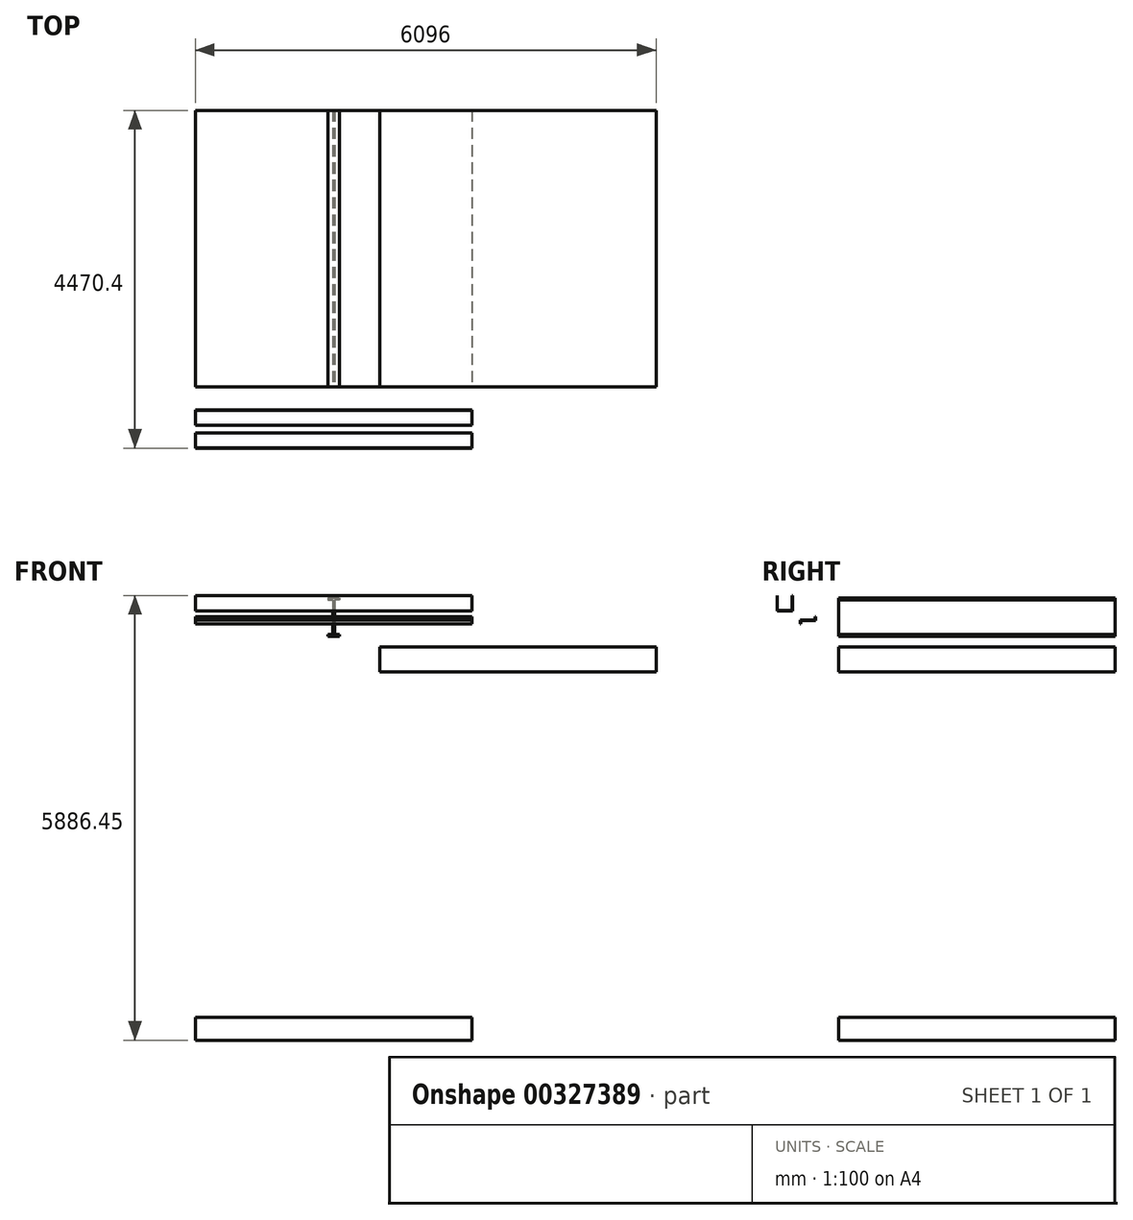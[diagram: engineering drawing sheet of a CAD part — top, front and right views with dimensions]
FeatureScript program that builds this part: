
annotation { "Feature Type Name" : "Feature", "Feature Type Description" : "" }
export const myFeature = defineFeature(function(context is Context, id is Id, definition is map)
    precondition{}
    {
        {
            var Q0;
            Q0=qCreatedBy(makeId("Front.planeOp"), FACE);
            var sketch = newSketch(context, id + "F0", { "sketchPlane" : qUnion([Q0])});
            skLineSegment(sketch, "E0.bottom", {"start": v(-1828.8, 0) * mm, "end": v(1828.8, 0) * mm});
            skLineSegment(sketch, "E0.top", {"start": v(-1828.8, -304.8) * mm, "end": v(1828.8, -304.8) * mm});
            skLineSegment(sketch, "E0.left", {"start": v(-1828.8, 0) * mm, "end": v(-1828.8, -304.8) * mm});
            skLineSegment(sketch, "E0.right", {"start": v(1828.8, 0) * mm, "end": v(1828.8, -304.8) * mm});
            skSolve(sketch);
        }
        {
            var Q0;
            Q0 = qSketchRegion(id + "F0", true);
            extrude(context, id + "F1", {"entities" : qUnion([Q0]), "oppositeDirection" : true, "depth" : 3657.6 * mm, "offsetDistance" : 25.4 * mm});
        }
        {
            var Q0;
            Q0=qCreatedBy(makeId("Front.planeOp"), FACE);
            var sketch = newSketch(context, id + "F2", { "sketchPlane" : qUnion([Q0])});
            skLineSegment(sketch, "E1.bottom", {"start": v(0, 5549.9) * mm, "end": v(76.2, 5549.9) * mm});
            skLineSegment(sketch, "E1.top", {"start": v(0, 5041.9) * mm, "end": v(76.2, 5041.9) * mm});
            skLineSegment(sketch, "E1.left", {"start": v(0, 5549.9) * mm, "end": v(0, 5041.9) * mm, "construction": true});
            skLineSegment(sketch, "E1.right", {"start": v(76.2, 5549.9) * mm, "end": v(76.2, 5524.5) * mm});
            skLineSegment(sketch, "E2.bottom", {"start": v(76.2, 5524.5) * mm, "end": v(12.7, 5524.5) * mm});
            skLineSegment(sketch, "E2.top", {"start": v(76.2, 5067.3) * mm, "end": v(12.7, 5067.3) * mm});
            skLineSegment(sketch, "E2.right", {"start": v(12.7, 5524.5) * mm, "end": v(12.7, 5067.3) * mm});
            skLineSegment(sketch, "E3.trimOffspring", {"start": v(76.2, 5067.3) * mm, "end": v(76.2, 5041.9) * mm});
            skLineSegment(sketch, "E4.MirrorCS", {"start": v(-76.2, 5549.9) * mm, "end": v(-76.2, 5524.5) * mm});
            skLineSegment(sketch, "E5.MirrorCS", {"start": v(-12.7, 5524.5) * mm, "end": v(-12.7, 5067.3) * mm});
            skLineSegment(sketch, "E6.MirrorCS", {"start": v(0, 5549.9) * mm, "end": v(-76.2, 5549.9) * mm});
            skLineSegment(sketch, "E7.MirrorCS", {"start": v(-76.2, 5067.3) * mm, "end": v(-76.2, 5041.9) * mm});
            skLineSegment(sketch, "E8.MirrorCS", {"start": v(0, 5041.9) * mm, "end": v(-76.2, 5041.9) * mm});
            skLineSegment(sketch, "E9.MirrorCS", {"start": v(-76.2, 5524.5) * mm, "end": v(-12.7, 5524.5) * mm});
            skLineSegment(sketch, "E10.MirrorCS", {"start": v(-76.2, 5067.3) * mm, "end": v(-12.7, 5067.3) * mm});
            skSolve(sketch);
        }
        {
            var Q0;
            Q0 = qSketchRegion(id + "F2", true);
            extrude(context, id + "F3", {"entities" : qUnion([Q0]), "oppositeDirection" : true, "depth" : 3657.6 * mm, "offsetDistance" : 25.4 * mm});
        }
        {
            var Q0;
            Q0=qCreatedBy(makeId("Right.planeOp"), FACE);
            var sketch = newSketch(context, id + "F4", { "sketchPlane" : qUnion([Q0])});
            skLineSegment(sketch, "E11.bottom", {"start": v(-508, 5207) * mm, "end": v(-501.65, 5207) * mm});
            skLineSegment(sketch, "E11.left", {"start": v(-508, 5207) * mm, "end": v(-508, 5251.45) * mm});
            skLineSegment(sketch, "E11.right", {"start": v(-501.65, 5207) * mm, "end": v(-501.65, 5251.45) * mm});
            skLineSegment(sketch, "E12.bottom", {"start": v(-501.65, 5251.45) * mm, "end": v(-311.15, 5251.45) * mm});
            skLineSegment(sketch, "E12.top", {"start": v(-508, 5257.8) * mm, "end": v(-311.15, 5257.8) * mm});
            skLineSegment(sketch, "E12.left", {"start": v(-508, 5251.45) * mm, "end": v(-508, 5257.8) * mm});
            skLineSegment(sketch, "E13.bottom", {"start": v(-311.15, 5251.45) * mm, "end": v(-304.8, 5251.45) * mm});
            skLineSegment(sketch, "E13.top", {"start": v(-311.15, 5302.25) * mm, "end": v(-304.8, 5302.25) * mm});
            skLineSegment(sketch, "E13.left", {"start": v(-311.15, 5257.8) * mm, "end": v(-311.15, 5302.25) * mm});
            skLineSegment(sketch, "E13.right", {"start": v(-304.8, 5251.45) * mm, "end": v(-304.8, 5302.25) * mm});
            skSolve(sketch);
        }
        {
            var Q0;
            Q0 = qSketchRegion(id + "F4", true);
            extrude(context, id + "F5", {"entities" : qUnion([Q0]), "depth" : 3657.6 * mm, "offsetDistance" : 25.4 * mm, "symmetric" : true});
        }
        {
            var Q0;
            Q0=qCreatedBy(makeId("Right.planeOp"), FACE);
            var sketch = newSketch(context, id + "F6", { "sketchPlane" : qUnion([Q0])});
            skLineSegment(sketch, "E14.bottom", {"start": v(-812.8, 5581.65) * mm, "end": v(-810.26, 5581.65) * mm});
            skLineSegment(sketch, "E14.top", {"start": v(-812.8, 5378.45) * mm, "end": v(-609.6, 5378.45) * mm});
            skLineSegment(sketch, "E14.left", {"start": v(-812.8, 5581.65) * mm, "end": v(-812.8, 5378.45) * mm});
            skLineSegment(sketch, "E14.right", {"start": v(-609.6, 5581.65) * mm, "end": v(-609.6, 5378.45) * mm});
            skLineSegment(sketch, "E15.top", {"start": v(-810.26, 5381) * mm, "end": v(-612.14, 5381) * mm});
            skLineSegment(sketch, "E15.left", {"start": v(-810.26, 5581.65) * mm, "end": v(-810.26, 5381) * mm});
            skLineSegment(sketch, "E15.right", {"start": v(-612.14, 5581.65) * mm, "end": v(-612.14, 5381) * mm});
            skLineSegment(sketch, "E16.trimOffspring", {"start": v(-612.14, 5581.65) * mm, "end": v(-609.6, 5581.65) * mm});
            skLineSegment(sketch, "E17", {"start": v(-810.26, 5381) * mm, "end": v(-810.26, 5378.45) * mm, "construction": true});
            skSolve(sketch);
        }
        {
            var Q0;
            Q0 = qSketchRegion(id + "F6", true);
            extrude(context, id + "F7", {"entities" : qUnion([Q0]), "depth" : 3657.6 * mm, "offsetDistance" : 25.4 * mm, "symmetric" : true});
        }
        {
            var Q0;
            Q0=qCreatedBy(makeId("Front.planeOp"), FACE);
            var sketch = newSketch(context, id + "F8", { "sketchPlane" : qUnion([Q0])});
            skLineSegment(sketch, "E18.bottom", {"start": v(609.6, 4902.2) * mm, "end": v(4267.2, 4902.2) * mm});
            skLineSegment(sketch, "E18.top", {"start": v(609.6, 4572) * mm, "end": v(4267.2, 4572) * mm});
            skLineSegment(sketch, "E18.left", {"start": v(609.6, 4902.2) * mm, "end": v(609.6, 4572) * mm});
            skLineSegment(sketch, "E18.right", {"start": v(4267.2, 4902.2) * mm, "end": v(4267.2, 4572) * mm});
            skSolve(sketch);
        }
        {
            var Q0;
            Q0 = qSketchRegion(id + "F8", true);
            extrude(context, id + "F9", {"entities" : qUnion([Q0]), "oppositeDirection" : true, "depth" : 3657.6 * mm, "offsetDistance" : 25.4 * mm});
        }
    });
